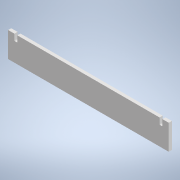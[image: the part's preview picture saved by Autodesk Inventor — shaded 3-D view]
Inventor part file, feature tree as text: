
AUTODESK INVENTOR PART (.ipt)
format: ipt  version: 2020 (Build 240168000, 168)  size: 116,736 bytes
history: native  units: in
note: dims shown in document units (in); Inventor stores cm internally (conversion verified against a paired STEP export)
features: extrude x1, sketch x1
ambient origin geometry x8: Origin, YZ Plane, XZ Plane, XY Plane, X Axis, Y Axis, Z Axis, Center Point
bodies: Solid1 (feature_tree)
feature tree (2):
  extrude  "Extrusion1"  Depth=2.0in
  sketch  "Sketch1"  dims[d0=12.7843in d1=2.0in d2=0.5in d3=0.5in d4=0.23in d5=0.5in d6=0.25in d7=0.0in d8=0.05in]
